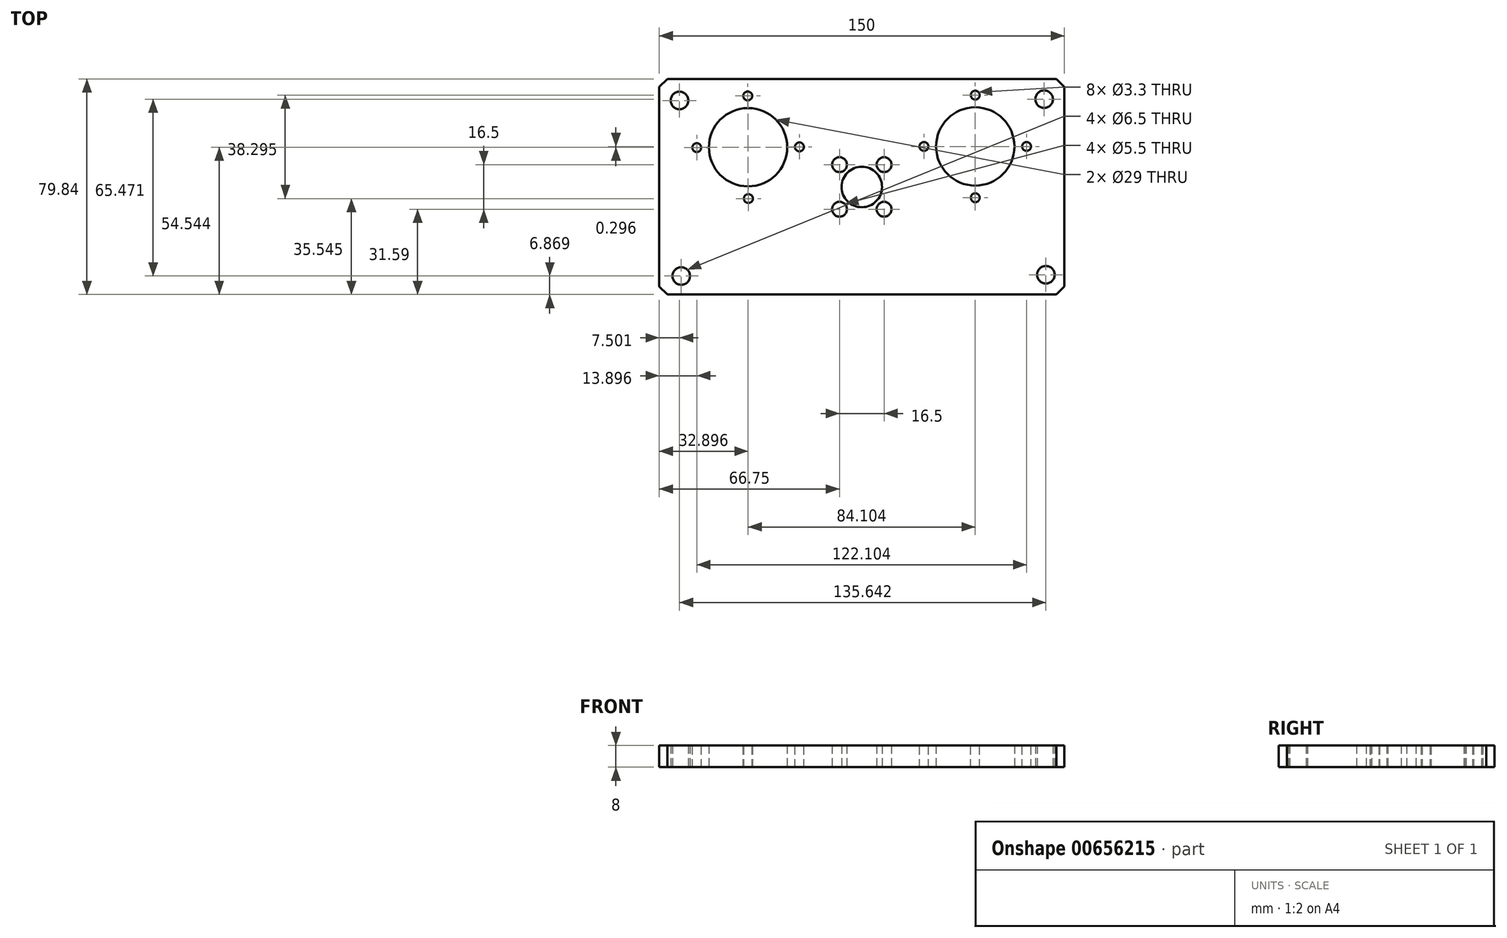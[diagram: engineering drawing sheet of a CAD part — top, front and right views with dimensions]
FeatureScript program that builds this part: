
annotation { "Feature Type Name" : "Feature", "Feature Type Description" : "" }
export const myFeature = defineFeature(function(context is Context, id is Id, definition is map)
    precondition{}
    {
        {
            var Q0;
            Q0=qCreatedBy(makeId("Top.planeOp"),FACE);
            var sketch = newSketch(context, id + "F0", { "sketchPlane" : qUnion([Q0])});
            skLineSegment(sketch, "E0.bottom", {"start": v(-75, 40) * mm, "end": v(75, 40) * mm});
            skLineSegment(sketch, "E0.top", {"start": v(-75, -39.84) * mm, "end": v(75, -39.84) * mm});
            skLineSegment(sketch, "E0.left", {"start": v(-75, 40) * mm, "end": v(-75, -39.84) * mm});
            skLineSegment(sketch, "E0.right", {"start": v(75, 40) * mm, "end": v(75, -39.84) * mm});
            skCircle(sketch, "E1", {"center": v(67.5, 32.5) * mm, "radius": 3.25 * mm});
            skCircle(sketch, "E2.0.1.0", {"center": v(68.14, -32.5) * mm, "radius": 3.25 * mm});
            skCircle(sketch, "E2.1.0.0", {"center": v(-67.5, 32.03) * mm, "radius": 3.25 * mm});
            skCircle(sketch, "E2.1.1.0", {"center": v(-66.86, -32.97) * mm, "radius": 3.25 * mm});
            skLineSegment(sketch, "E2.direction1", {"start": v(67.5, 32.5) * mm, "end": v(-67.5, 32.03) * mm, "construction": true});
            skLineSegment(sketch, "E2.direction2", {"start": v(67.5, 32.5) * mm, "end": v(68.14, -32.5) * mm, "construction": true});
            skCircle(sketch, "E3", {"center": v(0, 0) * mm, "radius": 7.5 * mm});
            skLineSegment(sketch, "E4.bottom", {"start": v(-8.25, 8.25) * mm, "end": v(8.25, 8.25) * mm, "construction": true});
            skLineSegment(sketch, "E4.top", {"start": v(-8.25, -8.25) * mm, "end": v(8.25, -8.25) * mm, "construction": true});
            skLineSegment(sketch, "E4.left", {"start": v(-8.25, 8.25) * mm, "end": v(-8.25, -8.25) * mm, "construction": true});
            skLineSegment(sketch, "E4.right", {"start": v(8.25, 8.25) * mm, "end": v(8.25, -8.25) * mm, "construction": true});
            skCircle(sketch, "E5", {"center": v(-8.25, 8.25) * mm, "radius": 2.75 * mm});
            skCircle(sketch, "E6.1.0", {"center": v(-8.25, -8.25) * mm, "radius": 2.75 * mm});
            skCircle(sketch, "E6.2.0", {"center": v(8.25, -8.25) * mm, "radius": 2.75 * mm});
            skCircle(sketch, "E6.3.0", {"center": v(8.25, 8.25) * mm, "radius": 2.75 * mm});
            skCircle(sketch, "E7", {"center": v(42, 15) * mm, "radius": 14.5 * mm});
            skCircle(sketch, "E8", {"center": v(23, 15) * mm, "radius": 1 * mm});
            skLineSegment(sketch, "E9", {"start": v(42, 15) * mm, "end": v(23, 15) * mm, "construction": true});
            skCircle(sketch, "E10.1.0", {"center": v(42, -4) * mm, "radius": 1 * mm});
            skCircle(sketch, "E10.2.0", {"center": v(61, 15) * mm, "radius": 1 * mm});
            skCircle(sketch, "E10.3.0", {"center": v(42, 34) * mm, "radius": 1 * mm});
            skLineSegment(sketch, "E11", {"start": v(0, 0) * mm, "end": v(-0.19, 53.35) * mm, "construction": true});
            skCircle(sketch, "E12.MirrorC", {"center": v(-42.1, 14.7) * mm, "radius": 14.5 * mm});
            skCircle(sketch, "E13.MirrorC", {"center": v(-42.24, 33.7) * mm, "radius": 1 * mm});
            skCircle(sketch, "E14.MirrorC", {"center": v(-23.1, 14.84) * mm, "radius": 1 * mm});
            skCircle(sketch, "E15.MirrorC", {"center": v(-41.97, -4.3) * mm, "radius": 1 * mm});
            skCircle(sketch, "E16.MirrorC", {"center": v(-61.1, 14.57) * mm, "radius": 1 * mm});
            skLineSegment(sketch, "E17.MirrorCS", {"start": v(-42.1, 14.7) * mm, "end": v(-23.1, 14.84) * mm, "construction": true});
            skSolve(sketch);
        }
        {
            var Q0;
            Q0=qSketchRegion(id+"F0",true);
            extrude(context, id + "F1", {"entities" : qUnion([Q0]), "depth" : 8 * mm, "offsetDistance" : 25 * mm});
        }
        {
            var Q0;
            Q0=makeQuery(id+"F1.opExtrude","SWEPT_EDGE",EDGE,{"disambiguationData":[OSD([sQuery(id+"F0.wireOp",EDGE,"E0.top"),sQuery(id+"F0.wireOp",EDGE,"E0.right")])]});
            var Q1;
            Q1=makeQuery(id+"F1.opExtrude","SWEPT_EDGE",EDGE,{"disambiguationData":[OSD([sQuery(id+"F0.wireOp",EDGE,"E0.bottom"),sQuery(id+"F0.wireOp",EDGE,"E0.right")])]});
            var Q2;
            Q2=makeQuery(id+"F1.opExtrude","SWEPT_EDGE",EDGE,{"disambiguationData":[OSD([sQuery(id+"F0.wireOp",EDGE,"E0.top"),sQuery(id+"F0.wireOp",EDGE,"E0.left")])]});
            var Q3;
            Q3=makeQuery(id+"F1.opExtrude","SWEPT_EDGE",EDGE,{"disambiguationData":[OSD([sQuery(id+"F0.wireOp",EDGE,"E0.bottom"),sQuery(id+"F0.wireOp",EDGE,"E0.left")])]});
            chamfer(context, id + "F2", {"entities" : qUnion([Q0, Q1, Q2, Q3]), "width" : 3 * mm, "tangentPropagation" : true});
        }
        {
            var Q0;
            Q0=makeQuery(id+"F1.opExtrude","CAP_FACE",FACE,{"disambiguationData":[OSD([sQuery(id+"F0.wireOp",EDGE,"E0.bottom"),sQuery(id+"F0.wireOp",EDGE,"E0.top"),sQuery(id+"F0.wireOp",EDGE,"E0.left"),sQuery(id+"F0.wireOp",EDGE,"E0.right"),sQuery(id+"F0.wireOp",EDGE,"E1"),sQuery(id+"F0.wireOp",EDGE,"E2.0.1.0"),sQuery(id+"F0.wireOp",EDGE,"E2.1.0.0"),sQuery(id+"F0.wireOp",EDGE,"E2.1.1.0"),sQuery(id+"F0.wireOp",EDGE,"E3"),sQuery(id+"F0.wireOp",EDGE,"E5"),sQuery(id+"F0.wireOp",EDGE,"E6.1.0"),sQuery(id+"F0.wireOp",EDGE,"E6.2.0"),sQuery(id+"F0.wireOp",EDGE,"E6.3.0"),sQuery(id+"F0.wireOp",EDGE,"E7"),sQuery(id+"F0.wireOp",EDGE,"E8"),sQuery(id+"F0.wireOp",EDGE,"E10.1.0"),sQuery(id+"F0.wireOp",EDGE,"E10.2.0"),sQuery(id+"F0.wireOp",EDGE,"E10.3.0"),sQuery(id+"F0.wireOp",EDGE,"E12.MirrorC"),sQuery(id+"F0.wireOp",EDGE,"E13.MirrorC"),sQuery(id+"F0.wireOp",EDGE,"E14.MirrorC"),sQuery(id+"F0.wireOp",EDGE,"E15.MirrorC"),sQuery(id+"F0.wireOp",EDGE,"E16.MirrorC")])],"isStart":false});
            var sketch = newSketch(context, id + "F3", { "sketchPlane" : qUnion([Q0])});
            skCircle(sketch, "E18", {"center": v(-42.24, 33.7) * mm, "radius": 1.42 * mm});
            skCircle(sketch, "E19", {"center": v(-61.1, 14.57) * mm, "radius": 1.32 * mm});
            skCircle(sketch, "E20", {"center": v(-23.1, 14.84) * mm, "radius": 1.48 * mm});
            skCircle(sketch, "E21", {"center": v(-41.97, -4.3) * mm, "radius": 1.49 * mm});
            skCircle(sketch, "E22", {"center": v(23, 15) * mm, "radius": 1.62 * mm});
            skCircle(sketch, "E23", {"center": v(42, 34) * mm, "radius": 1.5 * mm});
            skCircle(sketch, "E24", {"center": v(42, -4) * mm, "radius": 1.3 * mm});
            skCircle(sketch, "E25", {"center": v(61, 15) * mm, "radius": 1.37 * mm});
            skSolve(sketch);
        }
        {
            var Q0;
            Q0=sQuery(id+"F3.wireOp",VERTEX,"E23.center");
            var Q1;
            Q1=sQuery(id+"F3.wireOp",VERTEX,"E25.center");
            var Q2;
            Q2=sQuery(id+"F3.wireOp",VERTEX,"E24.center");
            var Q3;
            Q3=sQuery(id+"F3.wireOp",VERTEX,"E22.center");
            var Q4;
            Q4=sQuery(id+"F3.wireOp",VERTEX,"E20.center");
            var Q5;
            Q5=sQuery(id+"F3.wireOp",VERTEX,"E18.center");
            var Q6;
            Q6=sQuery(id+"F3.wireOp",VERTEX,"E21.center");
            var Q7;
            Q7=sQuery(id+"F3.wireOp",VERTEX,"E19.center");
            var Q8;
            Q8=makeQuery(id+"F1.opExtrude","SWEPT_BODY",BODY,{"disambiguationData":[OSD([sQuery(id+"F0.wireOp",EDGE,"E0.bottom"),sQuery(id+"F0.wireOp",EDGE,"E0.top"),sQuery(id+"F0.wireOp",EDGE,"E0.left"),sQuery(id+"F0.wireOp",EDGE,"E0.right"),sQuery(id+"F0.wireOp",EDGE,"E1"),sQuery(id+"F0.wireOp",EDGE,"E2.0.1.0"),sQuery(id+"F0.wireOp",EDGE,"E2.1.0.0"),sQuery(id+"F0.wireOp",EDGE,"E2.1.1.0"),sQuery(id+"F0.wireOp",EDGE,"E3"),sQuery(id+"F0.wireOp",EDGE,"E5"),sQuery(id+"F0.wireOp",EDGE,"E6.1.0"),sQuery(id+"F0.wireOp",EDGE,"E6.2.0"),sQuery(id+"F0.wireOp",EDGE,"E6.3.0"),sQuery(id+"F0.wireOp",EDGE,"E7"),sQuery(id+"F0.wireOp",EDGE,"E8"),sQuery(id+"F0.wireOp",EDGE,"E10.1.0"),sQuery(id+"F0.wireOp",EDGE,"E10.2.0"),sQuery(id+"F0.wireOp",EDGE,"E10.3.0"),sQuery(id+"F0.wireOp",EDGE,"E12.MirrorC"),sQuery(id+"F0.wireOp",EDGE,"E13.MirrorC"),sQuery(id+"F0.wireOp",EDGE,"E14.MirrorC"),sQuery(id+"F0.wireOp",EDGE,"E15.MirrorC"),sQuery(id+"F0.wireOp",EDGE,"E16.MirrorC")])]});
            hole(context, id + "F4", {"style" : HoleStyle.SIMPLE, "endStyle" : HoleEndStyle.THROUGH, "standardTappedOrClearance" : lookupTablePath({ "standard" : "ISO", "engagement" : "75%", "pitch" : "0.7 mm", "size" : "M4", "type" : "Tapped" }), "standardBlindInLast" : lookupTablePath({ "standard" : "ISO", "engagement" : "75%", "pitch" : "0.7 mm", "size" : "M4", "type" : "Tapped" }), "holeDiameter" : 3.3 * mm, "majorDiameter" : 4 * mm, "showTappedDepth" : true, "isTappedThrough" : true, "tappedDepth" : 15 * mm, "tapClearance" : 3, "locations" : qUnion([Q0, Q1, Q2, Q3, Q4, Q5, Q6, Q7]), "scope" : qUnion([Q8])});
        }
    });
